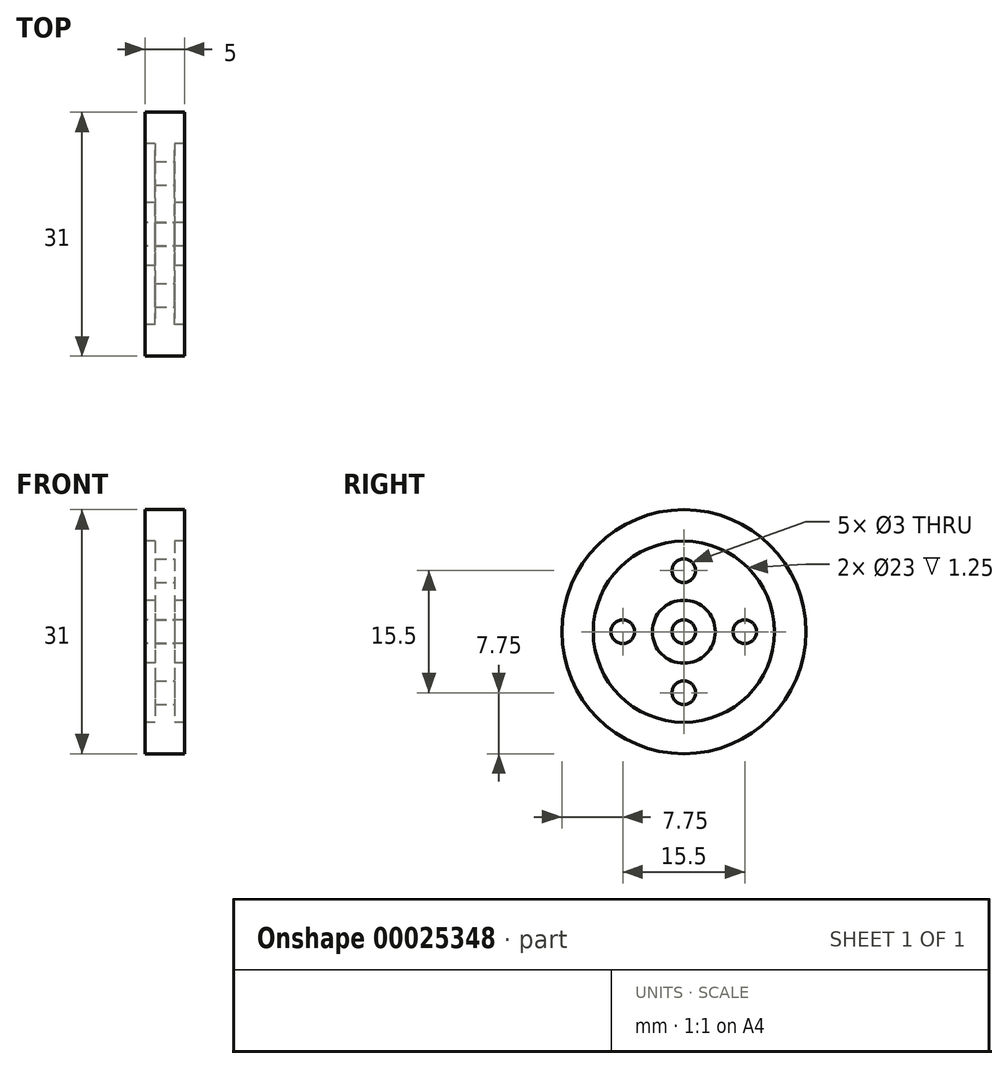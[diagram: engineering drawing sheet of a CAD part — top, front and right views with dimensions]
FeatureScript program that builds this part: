
annotation { "Feature Type Name" : "Feature", "Feature Type Description" : "" }
export const myFeature = defineFeature(function(context is Context, id is Id, definition is map)
    precondition{}
    {
        {
            var Q0;
            Q0=qCreatedBy(makeId("Front.planeOp"),FACE);
            var sketch = newSketch(context, id + "F0", { "sketchPlane" : qUnion([Q0])});
            skLineSegment(sketch, "E0", {"start": v(-50.28, 0) * mm, "end": v(50.2, 0) * mm, "construction": true});
            skLineSegment(sketch, "E1.rect.bottom", {"start": v(2.5, 4) * mm, "end": v(-2.5, 4) * mm});
            skLineSegment(sketch, "E1.rect.top", {"start": v(2.5, 1.5) * mm, "end": v(-2.5, 1.5) * mm});
            skLineSegment(sketch, "E1.rect.left", {"start": v(2.5, 4) * mm, "end": v(2.5, 1.5) * mm});
            skLineSegment(sketch, "E1.rect.right", {"start": v(-2.5, 4) * mm, "end": v(-2.5, 1.5) * mm});
            skPoint(sketch, "E1.rect.middle", {"position": v(0, 2.75) * mm});
            skLineSegment(sketch, "E2.bottom", {"start": v(-1.25, 4) * mm, "end": v(1.25, 4) * mm});
            skLineSegment(sketch, "E2.top", {"start": v(-1.25, 11.5) * mm, "end": v(1.25, 11.5) * mm});
            skLineSegment(sketch, "E2.left", {"start": v(-1.25, 4) * mm, "end": v(-1.25, 11.5) * mm});
            skLineSegment(sketch, "E2.right", {"start": v(1.25, 4) * mm, "end": v(1.25, 11.5) * mm});
            skLineSegment(sketch, "E3.rect.bottom", {"start": v(2.5, 11.5) * mm, "end": v(-2.5, 11.5) * mm});
            skLineSegment(sketch, "E3.rect.top", {"start": v(2.5, 15.5) * mm, "end": v(-2.5, 15.5) * mm});
            skLineSegment(sketch, "E3.rect.left", {"start": v(2.5, 11.5) * mm, "end": v(2.5, 15.5) * mm});
            skLineSegment(sketch, "E3.rect.right", {"start": v(-2.5, 11.5) * mm, "end": v(-2.5, 15.5) * mm});
            skPoint(sketch, "E3.rect.middle", {"position": v(0, 13.5) * mm});
            skSolve(sketch);
        }
        {
            var Q0;
            Q0 = qSketchRegion(id + "F0", true);
            var Q1;
            Q1=sQuery(id+"F0.wireOp",EDGE,"E0");
            revolve(context, id + "F1", {"entities" : qUnion([Q0]), "axis" : qUnion([Q1]), "revolveType" : RevolveType.FULL});
        }
        {
            var Q0;
            Q0=makeQuery(id+"F1.opRevolve","SWEPT_FACE",FACE,{"disambiguationData":[OSD([sQuery(id+"F0.wireOp",EDGE,"E3.rect.left")])]});
            var sketch = newSketch(context, id + "F2", { "sketchPlane" : qUnion([Q0])});
            skLineSegment(sketch, "E4", {"start": v(0, 0) * mm, "end": v(0, 15.5) * mm, "construction": true});
            skLineSegment(sketch, "E5", {"start": v(0, 15.5) * mm, "end": v(0, 0) * mm, "construction": true});
            skLineSegment(sketch, "E6", {"start": v(0, 0) * mm, "end": v(0, -15.5) * mm, "construction": true});
            skLineSegment(sketch, "E7", {"start": v(0, -15.5) * mm, "end": v(0, 0) * mm, "construction": true});
            skPoint(sketch, "E8", {"position": v(0, 7.75) * mm});
            skCircle(sketch, "E9", {"center": v(0, 0) * mm, "radius": 7.75 * mm, "construction": true});
            skCircle(sketch, "E10", {"center": v(0, 7.75) * mm, "radius": 1.5 * mm});
            skCircle(sketch, "E11", {"center": v(0, -7.75) * mm, "radius": 1.5 * mm});
            skLineSegment(sketch, "E12", {"start": v(15.5, 0) * mm, "end": v(-15.5, 0) * mm, "construction": true});
            skCircle(sketch, "E13", {"center": v(7.75, 0) * mm, "radius": 1.5 * mm});
            skCircle(sketch, "E14", {"center": v(-7.75, 0) * mm, "radius": 1.5 * mm});
            skSolve(sketch);
        }
        {
            var Q0;
            Q0 = qSketchRegion(id + "F2", true);
            extrude(context, id + "F3", {"entities" : qUnion([Q0]), "operationType" : NewBodyOperationType.REMOVE, "oppositeDirection" : true, "depth" : 25 * mm});
        }
    });
